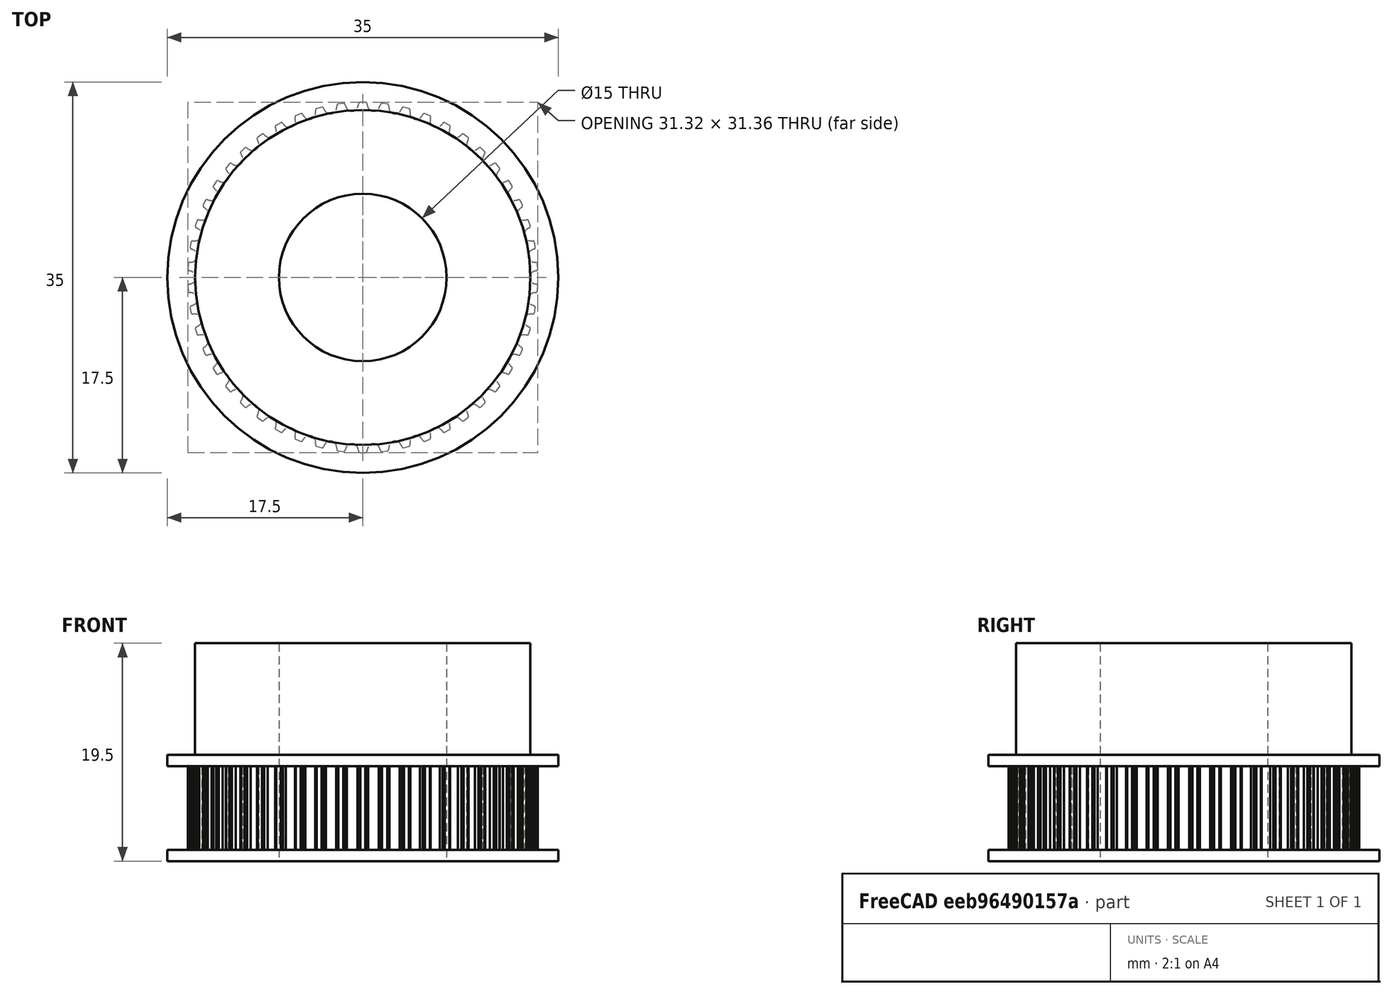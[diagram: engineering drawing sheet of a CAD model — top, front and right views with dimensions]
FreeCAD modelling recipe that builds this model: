
FCSTD DOCUMENT  (FreeCAD 1.0R39319 (Git))
Label: GT2_50
License: All rights reserved
LicenseURL: https://en.wikipedia.org/wiki/All_rights_reserved
objects: Sketcher::SketchObject×4, PartDesign::Pad×4, PartDesign::Body×1
note: 21 computed .brp shape members not serialized (recipe doc carries the construction recipe); baked Part::Feature solids carry a one-line shape summary decoded from their .brp

FEATURE [Sketcher::SketchObject] SketchGear
  ArcFitTolerance = 1e-06
  FullyConstrained = false
  MakeInternals = false
  MapMode = 5
  Placement = pos=(0,0,1) rot=(0,0,1;0rad)
  sketch-geometry (301):
    g0: ArcOfCircle CenterX=15.5115 CenterY=-0.75 CenterZ=0 NormalX=0 NormalY=0 NormalZ=1 AngleXU=1.11e-14 Radius=0.15 StartAngle=0 EndAngle=1.5708
    g1: ArcOfCircle CenterX=15.8575 CenterY=0.82798 CenterZ=0 NormalX=0 NormalY=0 NormalZ=-1 AngleXU=-1.3331 Radius=1.46929 StartAngle=0 EndAngle=0.255762
    g2: ArcOfCircle CenterX=15.4709 CenterY=0 CenterZ=0 NormalX=0 NormalY=0 NormalZ=-1 AngleXU=-0.984764 Radius=0.559359 StartAngle=0 EndAngle=1.96953
    g3: ArcOfCircle CenterX=15.8575 CenterY=-0.82798 CenterZ=0 NormalX=0 NormalY=0 NormalZ=-1 AngleXU=1.07734 Radius=1.46929 StartAngle=0 EndAngle=0.255762
    g4: ArcOfCircle CenterX=15.5115 CenterY=0.75 CenterZ=0 NormalX=0 NormalY=0 NormalZ=1 AngleXU=-1.5708 Radius=0.15 StartAngle=0 EndAngle=1.5708
    g5: LineSegment StartX=15.6615 StartY=0.75 StartZ=0 EndX=15.632 EndY=1.21882 EndZ=0
    g6: ArcOfCircle CenterX=15.4832 CenterY=1.20002 CenterZ=0 NormalX=0 NormalY=0 NormalZ=1 AngleXU=0.125664 Radius=0.15 StartAngle=0 EndAngle=1.5708
    g7: ArcOfCircle CenterX=15.6286 CenterY=2.80892 CenterZ=0 NormalX=0 NormalY=0 NormalZ=-1 AngleXU=-1.45876 Radius=1.46929 StartAngle=0 EndAngle=0.255762
    g8: ArcOfCircle CenterX=15.3489 CenterY=1.93901 CenterZ=0 NormalX=0 NormalY=0 NormalZ=-1 AngleXU=-1.11043 Radius=0.559359 StartAngle=0 EndAngle=1.96953
    g9: ArcOfCircle CenterX=15.8362 CenterY=1.16602 CenterZ=0 NormalX=0 NormalY=0 NormalZ=-1 AngleXU=0.951674 Radius=1.46929 StartAngle=0 EndAngle=0.255762
    g10: ArcOfCircle CenterX=15.2952 CenterY=2.68819 CenterZ=0 NormalX=0 NormalY=0 NormalZ=1 AngleXU=-1.44513 Radius=0.15 StartAngle=0 EndAngle=1.5708
    g11: LineSegment StartX=15.444 StartY=2.70699 StartZ=0 EndX=15.356 EndY=3.16842 EndZ=0
    g12: ArcOfCircle CenterX=15.2107 CenterY=3.13111 CenterZ=0 NormalX=0 NormalY=0 NormalZ=1 AngleXU=0.251327 Radius=0.15 StartAngle=0 EndAngle=1.5708
    g13: ArcOfCircle CenterX=15.1534 CenterY=4.74556 CenterZ=0 NormalX=0 NormalY=0 NormalZ=-1 AngleXU=-1.58443 Radius=1.46929 StartAngle=0 EndAngle=0.255762
    g14: ArcOfCircle CenterX=14.9848 CenterY=3.84744 CenterZ=0 NormalX=0 NormalY=0 NormalZ=-1 AngleXU=-1.23609 Radius=0.559359 StartAngle=0 EndAngle=1.96953
    g15: ArcOfCircle CenterX=15.5652 CenterY=3.14162 CenterZ=0 NormalX=0 NormalY=0 NormalZ=-1 AngleXU=0.82601 Radius=1.46929 StartAngle=0 EndAngle=0.255762
    g16: ArcOfCircle CenterX=14.8377 CenterY=4.58399 CenterZ=0 NormalX=0 NormalY=0 NormalZ=1 AngleXU=-1.31947 Radius=0.15 StartAngle=0 EndAngle=1.5708
    g17: LineSegment StartX=14.9829 StartY=4.62129 StartZ=0 EndX=14.8378 EndY=5.06805 EndZ=0
    g18: ArcOfCircle CenterX=14.6983 CenterY=5.01283 CenterZ=0 NormalX=0 NormalY=0 NormalZ=1 AngleXU=0.376991 Radius=0.15 StartAngle=0 EndAngle=1.5708
    g19: ArcOfCircle CenterX=14.4391 CenterY=6.60736 CenterZ=0 NormalX=0 NormalY=0 NormalZ=-1 AngleXU=-1.71009 Radius=1.46929 StartAngle=0 EndAngle=0.255762
    g20: ArcOfCircle CenterX=14.3844 CenterY=5.6952 CenterZ=0 NormalX=0 NormalY=0 NormalZ=-1 AngleXU=-1.36175 Radius=0.559359 StartAngle=0 EndAngle=1.96953
    g21: ArcOfCircle CenterX=15.0487 CenterY=5.06768 CenterZ=0 NormalX=0 NormalY=0 NormalZ=-1 AngleXU=0.700346 Radius=1.46929 StartAngle=0 EndAngle=0.255762
    g22: ArcOfCircle CenterX=14.1461 CenterY=6.40749 CenterZ=0 NormalX=0 NormalY=0 NormalZ=1 AngleXU=-1.19381 Radius=0.15 StartAngle=0 EndAngle=1.5708
    g23: LineSegment StartX=14.2856 StartY=6.46271 StartZ=0 EndX=14.0856 EndY=6.88775 EndZ=0
    g24: ArcOfCircle CenterX=13.9541 CenterY=6.81549 CenterZ=0 NormalX=0 NormalY=0 NormalZ=1 AngleXU=0.502655 Radius=0.15 StartAngle=0 EndAngle=1.5708
    g25: ArcOfCircle CenterX=13.4971 CenterY=8.36496 CenterZ=0 NormalX=0 NormalY=0 NormalZ=-1 AngleXU=-1.83575 Radius=1.46929 StartAngle=0 EndAngle=0.255762
    g26: ArcOfCircle CenterX=13.5572 CenterY=7.45314 CenterZ=0 NormalX=0 NormalY=0 NormalZ=-1 AngleXU=-1.48742 Radius=0.559359 StartAngle=0 EndAngle=1.96953
    g27: ArcOfCircle CenterX=14.2949 CenterY=6.91383 CenterZ=0 NormalX=0 NormalY=0 NormalZ=-1 AngleXU=0.574683 Radius=1.46929 StartAngle=0 EndAngle=0.255762
    g28: ArcOfCircle CenterX=13.2315 CenterY=8.12995 CenterZ=0 NormalX=0 NormalY=0 NormalZ=1 AngleXU=-1.06814 Radius=0.15 StartAngle=0 EndAngle=1.5708
    g29: LineSegment StartX=13.363 StartY=8.20221 StartZ=0 EndX=13.1113 EndY=8.59883 EndZ=0
    g30: ArcOfCircle CenterX=12.9899 CenterY=8.51066 CenterZ=0 NormalX=0 NormalY=0 NormalZ=1 AngleXU=0.628319 Radius=0.15 StartAngle=0 EndAngle=1.5708
    g31: ArcOfCircle CenterX=12.3423 CenterY=9.99063 CenterZ=0 NormalX=0 NormalY=0 NormalZ=-1 AngleXU=-1.96142 Radius=1.46929 StartAngle=0 EndAngle=0.255762
    g32: ArcOfCircle CenterX=12.5162 CenterY=9.09354 CenterZ=0 NormalX=0 NormalY=0 NormalZ=-1 AngleXU=-1.61308 Radius=0.559359 StartAngle=0 EndAngle=1.96953
    g33: ArcOfCircle CenterX=13.3156 CenterY=8.65093 CenterZ=0 NormalX=0 NormalY=0 NormalZ=-1 AngleXU=0.449019 Radius=1.46929 StartAngle=0 EndAngle=0.255762
    g34: ArcOfCircle CenterX=12.1082 CenterY=9.72419 CenterZ=0 NormalX=0 NormalY=0 NormalZ=1 AngleXU=-0.942478 Radius=0.15 StartAngle=0 EndAngle=1.5708
    g35: LineSegment StartX=12.2296 StartY=9.81236 StartZ=0 EndX=11.9301 EndY=10.1743 EndZ=0
    g36: ArcOfCircle CenterX=11.8208 CenterY=10.0716 CenterZ=0 NormalX=0 NormalY=0 NormalZ=1 AngleXU=0.753982 Radius=0.15 StartAngle=0 EndAngle=1.5708
    g37: ArcOfCircle CenterX=10.9928 CenterY=11.4588 CenterZ=0 NormalX=0 NormalY=0 NormalZ=-1 AngleXU=-2.08708 Radius=1.46929 StartAngle=0 EndAngle=0.255762
    g38: ArcOfCircle CenterX=11.2778 CenterY=10.5905 CenterZ=0 NormalX=0 NormalY=0 NormalZ=-1 AngleXU=-1.73875 Radius=0.559359 StartAngle=0 EndAngle=1.96953
    g39: ArcOfCircle CenterX=12.1264 CenterY=10.2516 CenterZ=0 NormalX=0 NormalY=0 NormalZ=-1 AngleXU=0.323355 Radius=1.46929 StartAngle=0 EndAngle=0.255762
    g40: ArcOfCircle CenterX=10.794 CenterY=11.1651 CenterZ=0 NormalX=0 NormalY=0 NormalZ=1 AngleXU=-0.816814 Radius=0.15 StartAngle=0 EndAngle=1.5708
    g41: LineSegment StartX=10.9033 StartY=11.2678 StartZ=0 EndX=10.5609 EndY=11.5893 EndZ=0
    g42: ArcOfCircle CenterX=10.4653 CenterY=11.4737 CenterZ=0 NormalX=0 NormalY=0 NormalZ=1 AngleXU=0.879646 Radius=0.15 StartAngle=0 EndAngle=1.5708
    g43: ArcOfCircle CenterX=9.46996 CenterY=12.7462 CenterZ=0 NormalX=0 NormalY=0 NormalZ=-1 AngleXU=-2.21275 Radius=1.46929 StartAngle=0 EndAngle=0.255762
    g44: ArcOfCircle CenterX=9.86149 CenterY=11.9205 CenterZ=0 NormalX=0 NormalY=0 NormalZ=-1 AngleXU=-1.86441 Radius=0.559359 StartAngle=0 EndAngle=1.96953
    g45: ArcOfCircle CenterX=10.7459 CenterY=11.6906 CenterZ=0 NormalX=0 NormalY=0 NormalZ=-1 AngleXU=0.197692 Radius=1.46929 StartAngle=0 EndAngle=0.255762
    g46: ArcOfCircle CenterX=9.30951 CenterY=12.4299 CenterZ=0 NormalX=0 NormalY=0 NormalZ=1 AngleXU=-0.69115 Radius=0.15 StartAngle=0 EndAngle=1.5708
    g47: LineSegment StartX=9.40513 StartY=12.5455 StartZ=0 EndX=9.02509 EndY=12.8216 EndZ=0
    g48: ArcOfCircle CenterX=8.94472 CenterY=12.6949 CenterZ=0 NormalX=0 NormalY=0 NormalZ=1 AngleXU=1.00531 Radius=0.15 StartAngle=0 EndAngle=1.5708
    g49: ArcOfCircle CenterX=7.79777 CenterY=13.8326 CenterZ=0 NormalX=0 NormalY=0 NormalZ=-1 AngleXU=-2.33841 Radius=1.46929 StartAngle=0 EndAngle=0.255762
    g50: ArcOfCircle CenterX=8.2897 CenterY=13.0625 CenterZ=0 NormalX=0 NormalY=0 NormalZ=-1 AngleXU=-1.99007 Radius=0.559359 StartAngle=0 EndAngle=1.96953
    g51: ArcOfCircle CenterX=9.19594 CenterY=12.9452 CenterZ=0 NormalX=0 NormalY=0 NormalZ=-1 AngleXU=0.0720278 Radius=1.46929 StartAngle=0 EndAngle=0.255762
    g52: ArcOfCircle CenterX=7.67823 CenterY=13.4987 CenterZ=0 NormalX=0 NormalY=0 NormalZ=1 AngleXU=-0.565487 Radius=0.15 StartAngle=0 EndAngle=1.5708
    g53: LineSegment StartX=7.7586 StartY=13.6253 StartZ=0 EndX=7.34696 EndY=13.8516 EndZ=0
    g54: ArcOfCircle CenterX=7.28309 CenterY=13.7159 CenterZ=0 NormalX=0 NormalY=0 NormalZ=1 AngleXU=1.13097 Radius=0.15 StartAngle=0 EndAngle=1.5708
    g55: ArcOfCircle CenterX=6.0026 CenterY=14.7008 CenterZ=0 NormalX=0 NormalY=0 NormalZ=-1 AngleXU=-2.46407 Radius=1.46929 StartAngle=0 EndAngle=0.255762
    g56: ArcOfCircle CenterX=6.58717 CenterY=13.9984 CenterZ=0 NormalX=0 NormalY=0 NormalZ=-1 AngleXU=-2.11574 Radius=0.559359 StartAngle=0 EndAngle=1.96953
    g57: ArcOfCircle CenterX=7.50096 CenterY=13.9957 CenterZ=0 NormalX=0 NormalY=0 NormalZ=-1 AngleXU=-0.0536359 Radius=1.46929 StartAngle=0 EndAngle=0.255762
    g58: ArcOfCircle CenterX=5.92585 CenterY=14.3546 CenterZ=0 NormalX=0 NormalY=0 NormalZ=1 AngleXU=-0.439823 Radius=0.15 StartAngle=0 EndAngle=1.5708
    g59: LineSegment StartX=5.98972 StartY=14.4903 StartZ=0 EndX=5.55296 EndY=14.6632 EndZ=0
    g60: ArcOfCircle CenterX=5.50661 CenterY=14.5205 CenterZ=0 NormalX=0 NormalY=0 NormalZ=1 AngleXU=1.25664 Radius=0.15 StartAngle=0 EndAngle=1.5708
    g61: ArcOfCircle CenterX=4.11277 CenterY=15.3372 CenterZ=0 NormalX=0 NormalY=0 NormalZ=-1 AngleXU=-2.58974 Radius=1.46929 StartAngle=0 EndAngle=0.255762
    g62: ArcOfCircle CenterX=4.78076 CenterY=14.7137 CenterZ=0 NormalX=0 NormalY=0 NormalZ=-1 AngleXU=-2.2414 Radius=0.559359 StartAngle=0 EndAngle=1.96953
    g63: ArcOfCircle CenterX=5.68768 CenterY=14.8255 CenterZ=0 NormalX=0 NormalY=0 NormalZ=-1 AngleXU=-0.1793 Radius=1.46929 StartAngle=0 EndAngle=0.255762
    g64: ArcOfCircle CenterX=4.08002 CenterY=14.9841 CenterZ=0 NormalX=0 NormalY=0 NormalZ=1 AngleXU=-0.314159 Radius=0.15 StartAngle=0 EndAngle=1.5708
    g65: LineSegment StartX=4.12638 StartY=15.1267 StartZ=0 EndX=3.67139 EndY=15.2436 EndZ=0
    g66: ArcOfCircle CenterX=3.64328 CenterY=15.0962 CenterZ=0 NormalX=0 NormalY=0 NormalZ=1 AngleXU=1.3823 Radius=0.15 StartAngle=0 EndAngle=1.5708
    g67: ArcOfCircle CenterX=2.15808 CenterY=15.7317 CenterZ=0 NormalX=0 NormalY=0 NormalZ=-1 AngleXU=-2.7154 Radius=1.46929 StartAngle=0 EndAngle=0.255762
    g68: ArcOfCircle CenterX=2.89895 CenterY=15.1968 CenterZ=0 NormalX=0 NormalY=0 NormalZ=-1 AngleXU=-2.36706 Radius=0.559359 StartAngle=0 EndAngle=1.96953
    g69: ArcOfCircle CenterX=3.78471 CenterY=15.4214 CenterZ=0 NormalX=0 NormalY=0 NormalZ=-1 AngleXU=-0.304963 Radius=1.46929 StartAngle=0 EndAngle=0.255762
    g70: ArcOfCircle CenterX=2.16985 CenterY=15.3773 CenterZ=0 NormalX=0 NormalY=0 NormalZ=1 AngleXU=-0.188496 Radius=0.15 StartAngle=0 EndAngle=1.5708
    g71: LineSegment StartX=2.19796 StartY=15.5246 StartZ=0 EndX=1.73191 EndY=15.5835 EndZ=0
    g72: ArcOfCircle CenterX=1.72249 CenterY=15.4338 CenterZ=0 NormalX=0 NormalY=0 NormalZ=1 AngleXU=1.50796 Radius=0.15 StartAngle=0 EndAngle=1.5708
    g73: ArcOfCircle CenterX=0.169352 CenterY=15.8782 CenterZ=0 NormalX=0 NormalY=0 NormalZ=-1 AngleXU=-2.84106 Radius=1.46929 StartAngle=0 EndAngle=0.255762
    g74: ArcOfCircle CenterX=0.971423 CenterY=15.4403 CenterZ=0 NormalX=0 NormalY=0 NormalZ=-1 AngleXU=-2.49273 Radius=0.559359 StartAngle=0 EndAngle=1.96953
    g75: ArcOfCircle CenterX=1.82204 CenterY=15.7742 CenterZ=0 NormalX=0 NormalY=0 NormalZ=-1 AngleXU=-0.430627 Radius=1.46929 StartAngle=0 EndAngle=0.255762
    g76: ArcOfCircle CenterX=0.225455 CenterY=15.528 CenterZ=0 NormalX=0 NormalY=0 NormalZ=1 AngleXU=-0.0628319 Radius=0.15 StartAngle=0 EndAngle=1.5708
    g77: LineSegment StartX=0.234873 StartY=15.6777 StartZ=0 EndX=-0.234873 EndY=15.6777 EndZ=0
    g78: ArcOfCircle CenterX=-0.225455 CenterY=15.528 CenterZ=0 NormalX=0 NormalY=0 NormalZ=1 AngleXU=1.63363 Radius=0.15 StartAngle=0 EndAngle=1.5708
    g79: ArcOfCircle CenterX=-1.82204 CenterY=15.7742 CenterZ=0 NormalX=0 NormalY=0 NormalZ=-1 AngleXU=-2.96673 Radius=1.46929 StartAngle=0 EndAngle=0.255762
    g80: ArcOfCircle CenterX=-0.971423 CenterY=15.4403 CenterZ=0 NormalX=0 NormalY=0 NormalZ=-1 AngleXU=-2.61839 Radius=0.559359 StartAngle=0 EndAngle=1.96953
    g81: ArcOfCircle CenterX=-0.169352 CenterY=15.8782 CenterZ=0 NormalX=0 NormalY=0 NormalZ=-1 AngleXU=-0.556291 Radius=1.46929 StartAngle=0 EndAngle=0.255762
    g82: ArcOfCircle CenterX=-1.72249 CenterY=15.4338 CenterZ=0 NormalX=0 NormalY=0 NormalZ=1 AngleXU=0.0628319 Radius=0.15 StartAngle=0 EndAngle=1.5708
    g83: LineSegment StartX=-1.73191 StartY=15.5835 StartZ=0 EndX=-2.19796 EndY=15.5246 EndZ=0
    g84: ArcOfCircle CenterX=-2.16985 CenterY=15.3773 CenterZ=0 NormalX=0 NormalY=0 NormalZ=1 AngleXU=1.75929 Radius=0.15 StartAngle=0 EndAngle=1.5708
    g85: ArcOfCircle CenterX=-3.78471 CenterY=15.4214 CenterZ=0 NormalX=0 NormalY=0 NormalZ=-1 AngleXU=-3.09239 Radius=1.46929 StartAngle=0 EndAngle=0.255762
    g86: ArcOfCircle CenterX=-2.89895 CenterY=15.1968 CenterZ=0 NormalX=0 NormalY=0 NormalZ=-1 AngleXU=-2.74406 Radius=0.559359 StartAngle=0 EndAngle=1.96953
    g87: ArcOfCircle CenterX=-2.15808 CenterY=15.7317 CenterZ=0 NormalX=0 NormalY=0 NormalZ=-1 AngleXU=-0.681954 Radius=1.46929 StartAngle=0 EndAngle=0.255762
    g88: ArcOfCircle CenterX=-3.64328 CenterY=15.0962 CenterZ=0 NormalX=0 NormalY=0 NormalZ=1 AngleXU=0.188496 Radius=0.15 StartAngle=0 EndAngle=1.5708
    g89: LineSegment StartX=-3.67139 StartY=15.2436 StartZ=0 EndX=-4.12638 EndY=15.1267 EndZ=0
    g90: ArcOfCircle CenterX=-4.08002 CenterY=14.9841 CenterZ=0 NormalX=0 NormalY=0 NormalZ=1 AngleXU=1.88496 Radius=0.15 StartAngle=0 EndAngle=1.5708
    g91: ArcOfCircle CenterX=-5.68768 CenterY=14.8255 CenterZ=0 NormalX=0 NormalY=0 NormalZ=-1 AngleXU=3.06513 Radius=1.46929 StartAngle=0 EndAngle=0.255762
    g92: ArcOfCircle CenterX=-4.78076 CenterY=14.7137 CenterZ=0 NormalX=0 NormalY=0 NormalZ=-1 AngleXU=-2.86972 Radius=0.559359 StartAngle=0 EndAngle=1.96953
    g93: ArcOfCircle CenterX=-4.11277 CenterY=15.3372 CenterZ=0 NormalX=0 NormalY=0 NormalZ=-1 AngleXU=-0.807618 Radius=1.46929 StartAngle=0 EndAngle=0.255762
    g94: ArcOfCircle CenterX=-5.50661 CenterY=14.5205 CenterZ=0 NormalX=0 NormalY=0 NormalZ=1 AngleXU=0.314159 Radius=0.15 StartAngle=0 EndAngle=1.5708
    g95: LineSegment StartX=-5.55296 StartY=14.6632 StartZ=0 EndX=-5.98972 EndY=14.4903 EndZ=0
    g96: ArcOfCircle CenterX=-5.92585 CenterY=14.3546 CenterZ=0 NormalX=0 NormalY=0 NormalZ=1 AngleXU=2.01062 Radius=0.15 StartAngle=0 EndAngle=1.5708
    g97: ArcOfCircle CenterX=-7.50096 CenterY=13.9957 CenterZ=0 NormalX=0 NormalY=0 NormalZ=-1 AngleXU=2.93947 Radius=1.46929 StartAngle=0 EndAngle=0.255762
    g98: ArcOfCircle CenterX=-6.58717 CenterY=13.9984 CenterZ=0 NormalX=0 NormalY=0 NormalZ=-1 AngleXU=-2.99538 Radius=0.559359 StartAngle=0 EndAngle=1.96953
    g99: ArcOfCircle CenterX=-6.0026 CenterY=14.7008 CenterZ=0 NormalX=0 NormalY=0 NormalZ=-1 AngleXU=-0.933282 Radius=1.46929 StartAngle=0 EndAngle=0.255762
    g100: ArcOfCircle CenterX=-7.28309 CenterY=13.7159 CenterZ=0 NormalX=0 NormalY=0 NormalZ=1 AngleXU=0.439823 Radius=0.15 StartAngle=0 EndAngle=1.5708
    g101: LineSegment StartX=-7.34696 StartY=13.8516 StartZ=0 EndX=-7.7586 EndY=13.6253 EndZ=0
    g102: ArcOfCircle CenterX=-7.67823 CenterY=13.4987 CenterZ=0 NormalX=0 NormalY=0 NormalZ=1 AngleXU=2.13628 Radius=0.15 StartAngle=0 EndAngle=1.5708
    g103: ArcOfCircle CenterX=-9.19594 CenterY=12.9452 CenterZ=0 NormalX=0 NormalY=0 NormalZ=-1 AngleXU=2.8138 Radius=1.46929 StartAngle=0 EndAngle=0.255762
    g104: ArcOfCircle CenterX=-8.2897 CenterY=13.0625 CenterZ=0 NormalX=0 NormalY=0 NormalZ=-1 AngleXU=-3.12105 Radius=0.559359 StartAngle=0 EndAngle=1.96953
    g105: ArcOfCircle CenterX=-7.79777 CenterY=13.8326 CenterZ=0 NormalX=0 NormalY=0 NormalZ=-1 AngleXU=-1.05895 Radius=1.46929 StartAngle=0 EndAngle=0.255762
    g106: ArcOfCircle CenterX=-8.94472 CenterY=12.6949 CenterZ=0 NormalX=0 NormalY=0 NormalZ=1 AngleXU=0.565487 Radius=0.15 StartAngle=0 EndAngle=1.5708
    g107: LineSegment StartX=-9.02509 StartY=12.8216 StartZ=0 EndX=-9.40513 EndY=12.5455 EndZ=0
    g108: ArcOfCircle CenterX=-9.30951 CenterY=12.4299 CenterZ=0 NormalX=0 NormalY=0 NormalZ=1 AngleXU=2.26195 Radius=0.15 StartAngle=0 EndAngle=1.5708
    g109: ArcOfCircle CenterX=-10.7459 CenterY=11.6906 CenterZ=0 NormalX=0 NormalY=0 NormalZ=-1 AngleXU=2.68814 Radius=1.46929 StartAngle=0 EndAngle=0.255762
    g110: ArcOfCircle CenterX=-9.86149 CenterY=11.9205 CenterZ=0 NormalX=0 NormalY=0 NormalZ=-1 AngleXU=3.03648 Radius=0.559359 StartAngle=0 EndAngle=1.96953
    g111: ArcOfCircle CenterX=-9.46996 CenterY=12.7462 CenterZ=0 NormalX=0 NormalY=0 NormalZ=-1 AngleXU=-1.18461 Radius=1.46929 StartAngle=0 EndAngle=0.255762
    g112: ArcOfCircle CenterX=-10.4653 CenterY=11.4737 CenterZ=0 NormalX=0 NormalY=0 NormalZ=1 AngleXU=0.69115 Radius=0.15 StartAngle=0 EndAngle=1.5708
    g113: LineSegment StartX=-10.5609 StartY=11.5893 StartZ=0 EndX=-10.9033 EndY=11.2678 EndZ=0
    g114: ArcOfCircle CenterX=-10.794 CenterY=11.1651 CenterZ=0 NormalX=0 NormalY=0 NormalZ=1 AngleXU=2.38761 Radius=0.15 StartAngle=0 EndAngle=1.5708
    g115: ArcOfCircle CenterX=-12.1264 CenterY=10.2516 CenterZ=0 NormalX=0 NormalY=0 NormalZ=-1 AngleXU=2.56248 Radius=1.46929 StartAngle=0 EndAngle=0.255762
    g116: ArcOfCircle CenterX=-11.2778 CenterY=10.5905 CenterZ=0 NormalX=0 NormalY=0 NormalZ=-1 AngleXU=2.91081 Radius=0.559359 StartAngle=0 EndAngle=1.96953
    g117: ArcOfCircle CenterX=-10.9928 CenterY=11.4588 CenterZ=0 NormalX=0 NormalY=0 NormalZ=-1 AngleXU=-1.31027 Radius=1.46929 StartAngle=0 EndAngle=0.255762
    g118: ArcOfCircle CenterX=-11.8208 CenterY=10.0716 CenterZ=0 NormalX=0 NormalY=0 NormalZ=1 AngleXU=0.816814 Radius=0.15 StartAngle=0 EndAngle=1.5708
    g119: LineSegment StartX=-11.9301 StartY=10.1743 StartZ=0 EndX=-12.2296 EndY=9.81236 EndZ=0
    g120: ArcOfCircle CenterX=-12.1082 CenterY=9.72419 CenterZ=0 NormalX=0 NormalY=0 NormalZ=1 AngleXU=2.51327 Radius=0.15 StartAngle=0 EndAngle=1.5708
    g121: ArcOfCircle CenterX=-13.3156 CenterY=8.65093 CenterZ=0 NormalX=0 NormalY=0 NormalZ=-1 AngleXU=2.43681 Radius=1.46929 StartAngle=0 EndAngle=0.255762
    g122: ArcOfCircle CenterX=-12.5162 CenterY=9.09354 CenterZ=0 NormalX=0 NormalY=0 NormalZ=-1 AngleXU=2.78515 Radius=0.559359 StartAngle=0 EndAngle=1.96953
    g123: ArcOfCircle CenterX=-12.3423 CenterY=9.99063 CenterZ=0 NormalX=0 NormalY=0 NormalZ=-1 AngleXU=-1.43594 Radius=1.46929 StartAngle=0 EndAngle=0.255762
    g124: ArcOfCircle CenterX=-12.9899 CenterY=8.51066 CenterZ=0 NormalX=0 NormalY=0 NormalZ=1 AngleXU=0.942478 Radius=0.15 StartAngle=0 EndAngle=1.5708
    g125: LineSegment StartX=-13.1113 StartY=8.59883 StartZ=0 EndX=-13.363 EndY=8.20221 EndZ=0
    g126: ArcOfCircle CenterX=-13.2315 CenterY=8.12995 CenterZ=0 NormalX=0 NormalY=0 NormalZ=1 AngleXU=2.63894 Radius=0.15 StartAngle=0 EndAngle=1.5708
    g127: ArcOfCircle CenterX=-14.2949 CenterY=6.91383 CenterZ=0 NormalX=0 NormalY=0 NormalZ=-1 AngleXU=2.31115 Radius=1.46929 StartAngle=0 EndAngle=0.255762
    g128: ArcOfCircle CenterX=-13.5572 CenterY=7.45314 CenterZ=0 NormalX=0 NormalY=0 NormalZ=-1 AngleXU=2.65948 Radius=0.559359 StartAngle=0 EndAngle=1.96953
    g129: ArcOfCircle CenterX=-13.4971 CenterY=8.36496 CenterZ=0 NormalX=0 NormalY=0 NormalZ=-1 AngleXU=-1.5616 Radius=1.46929 StartAngle=0 EndAngle=0.255762
    g130: ArcOfCircle CenterX=-13.9541 CenterY=6.81549 CenterZ=0 NormalX=0 NormalY=0 NormalZ=1 AngleXU=1.06814 Radius=0.15 StartAngle=0 EndAngle=1.5708
    g131: LineSegment StartX=-14.0856 StartY=6.88775 StartZ=0 EndX=-14.2856 EndY=6.46271 EndZ=0
    g132: ArcOfCircle CenterX=-14.1461 CenterY=6.40749 CenterZ=0 NormalX=0 NormalY=0 NormalZ=1 AngleXU=2.7646 Radius=0.15 StartAngle=0 EndAngle=1.5708
    g133: ArcOfCircle CenterX=-15.0487 CenterY=5.06768 CenterZ=0 NormalX=0 NormalY=0 NormalZ=-1 AngleXU=2.18548 Radius=1.46929 StartAngle=0 EndAngle=0.255762
    g134: ArcOfCircle CenterX=-14.3844 CenterY=5.6952 CenterZ=0 NormalX=0 NormalY=0 NormalZ=-1 AngleXU=2.53382 Radius=0.559359 StartAngle=0 EndAngle=1.96953
    g135: ArcOfCircle CenterX=-14.4391 CenterY=6.60736 CenterZ=0 NormalX=0 NormalY=0 NormalZ=-1 AngleXU=-1.68726 Radius=1.46929 StartAngle=0 EndAngle=0.255762
    g136: ArcOfCircle CenterX=-14.6983 CenterY=5.01283 CenterZ=0 NormalX=0 NormalY=0 NormalZ=1 AngleXU=1.19381 Radius=0.15 StartAngle=0 EndAngle=1.5708
    g137: LineSegment StartX=-14.8378 StartY=5.06805 StartZ=0 EndX=-14.9829 EndY=4.62129 EndZ=0
    g138: ArcOfCircle CenterX=-14.8377 CenterY=4.58399 CenterZ=0 NormalX=0 NormalY=0 NormalZ=1 AngleXU=2.89027 Radius=0.15 StartAngle=0 EndAngle=1.5708
    g139: ArcOfCircle CenterX=-15.5652 CenterY=3.14162 CenterZ=0 NormalX=0 NormalY=0 NormalZ=-1 AngleXU=2.05982 Radius=1.46929 StartAngle=0 EndAngle=0.255762
    g140: ArcOfCircle CenterX=-14.9848 CenterY=3.84744 CenterZ=0 NormalX=0 NormalY=0 NormalZ=-1 AngleXU=2.40816 Radius=0.559359 StartAngle=0 EndAngle=1.96953
    g141: ArcOfCircle CenterX=-15.1534 CenterY=4.74556 CenterZ=0 NormalX=0 NormalY=0 NormalZ=-1 AngleXU=-1.81293 Radius=1.46929 StartAngle=0 EndAngle=0.255762
    g142: ArcOfCircle CenterX=-15.2107 CenterY=3.13111 CenterZ=0 NormalX=0 NormalY=0 NormalZ=1 AngleXU=1.31947 Radius=0.15 StartAngle=0 EndAngle=1.5708
    g143: LineSegment StartX=-15.356 StartY=3.16842 StartZ=0 EndX=-15.444 EndY=2.70699 EndZ=0
    g144: ArcOfCircle CenterX=-15.2952 CenterY=2.68819 CenterZ=0 NormalX=0 NormalY=0 NormalZ=1 AngleXU=3.01593 Radius=0.15 StartAngle=0 EndAngle=1.5708
    g145: ArcOfCircle CenterX=-15.8362 CenterY=1.16602 CenterZ=0 NormalX=0 NormalY=0 NormalZ=-1 AngleXU=1.93416 Radius=1.46929 StartAngle=0 EndAngle=0.255762
    g146: ArcOfCircle CenterX=-15.3489 CenterY=1.93901 CenterZ=0 NormalX=0 NormalY=0 NormalZ=-1 AngleXU=2.28249 Radius=0.559359 StartAngle=0 EndAngle=1.96953
    g147: ArcOfCircle CenterX=-15.6286 CenterY=2.80892 CenterZ=0 NormalX=0 NormalY=0 NormalZ=-1 AngleXU=-1.93859 Radius=1.46929 StartAngle=0 EndAngle=0.255762
    g148: ArcOfCircle CenterX=-15.4832 CenterY=1.20002 CenterZ=0 NormalX=0 NormalY=0 NormalZ=1 AngleXU=1.44513 Radius=0.15 StartAngle=0 EndAngle=1.5708
    g149: LineSegment StartX=-15.632 StartY=1.21882 StartZ=0 EndX=-15.6615 EndY=0.75 EndZ=0
    g150: ArcOfCircle CenterX=-15.5115 CenterY=0.75 CenterZ=0 NormalX=0 NormalY=0 NormalZ=1 AngleXU=-3.14159 Radius=0.15 StartAngle=0 EndAngle=1.5708
    g151: ArcOfCircle CenterX=-15.8575 CenterY=-0.82798 CenterZ=0 NormalX=0 NormalY=0 NormalZ=-1 AngleXU=1.80849 Radius=1.46929 StartAngle=0 EndAngle=0.255762
    g152: ArcOfCircle CenterX=-15.4709 CenterY=1.8e-15 CenterZ=0 NormalX=0 NormalY=0 NormalZ=-1 AngleXU=2.15683 Radius=0.559359 StartAngle=0 EndAngle=1.96953
    g153: ArcOfCircle CenterX=-15.8575 CenterY=0.82798 CenterZ=0 NormalX=0 NormalY=0 NormalZ=-1 AngleXU=-2.06426 Radius=1.46929 StartAngle=0 EndAngle=0.255762
    g154: ArcOfCircle CenterX=-15.5115 CenterY=-0.75 CenterZ=0 NormalX=0 NormalY=0 NormalZ=1 AngleXU=1.5708 Radius=0.15 StartAngle=0 EndAngle=1.5708
    g155: LineSegment StartX=-15.6615 StartY=-0.75 StartZ=0 EndX=-15.632 EndY=-1.21882 EndZ=0
    g156: ArcOfCircle CenterX=-15.4832 CenterY=-1.20002 CenterZ=0 NormalX=0 NormalY=0 NormalZ=1 AngleXU=-3.01593 Radius=0.15 StartAngle=0 EndAngle=1.5708
    g157: ArcOfCircle CenterX=-15.6286 CenterY=-2.80892 CenterZ=0 NormalX=0 NormalY=0 NormalZ=-1 AngleXU=1.68283 Radius=1.46929 StartAngle=0 EndAngle=0.255762
    g158: ArcOfCircle CenterX=-15.3489 CenterY=-1.93901 CenterZ=0 NormalX=0 NormalY=0 NormalZ=-1 AngleXU=2.03117 Radius=0.559359 StartAngle=0 EndAngle=1.96953
    g159: ArcOfCircle CenterX=-15.8362 CenterY=-1.16602 CenterZ=0 NormalX=0 NormalY=0 NormalZ=-1 AngleXU=-2.18992 Radius=1.46929 StartAngle=0 EndAngle=0.255762
    g160: ArcOfCircle CenterX=-15.2952 CenterY=-2.68819 CenterZ=0 NormalX=0 NormalY=0 NormalZ=1 AngleXU=1.69646 Radius=0.15 StartAngle=0 EndAngle=1.5708
    g161: LineSegment StartX=-15.444 StartY=-2.70699 StartZ=0 EndX=-15.356 EndY=-3.16842 EndZ=0
    g162: ArcOfCircle CenterX=-15.2107 CenterY=-3.13111 CenterZ=0 NormalX=0 NormalY=0 NormalZ=1 AngleXU=-2.89027 Radius=0.15 StartAngle=0 EndAngle=1.5708
    g163: ArcOfCircle CenterX=-15.1534 CenterY=-4.74556 CenterZ=0 NormalX=0 NormalY=0 NormalZ=-1 AngleXU=1.55717 Radius=1.46929 StartAngle=0 EndAngle=0.255762
    g164: ArcOfCircle CenterX=-14.9848 CenterY=-3.84744 CenterZ=0 NormalX=0 NormalY=0 NormalZ=-1 AngleXU=1.9055 Radius=0.559359 StartAngle=0 EndAngle=1.96953
    g165: ArcOfCircle CenterX=-15.5652 CenterY=-3.14162 CenterZ=0 NormalX=0 NormalY=0 NormalZ=-1 AngleXU=-2.31558 Radius=1.46929 StartAngle=0 EndAngle=0.255762
    g166: ArcOfCircle CenterX=-14.8377 CenterY=-4.58399 CenterZ=0 NormalX=0 NormalY=0 NormalZ=1 AngleXU=1.82212 Radius=0.15 StartAngle=0 EndAngle=1.5708
    g167: LineSegment StartX=-14.9829 StartY=-4.62129 StartZ=0 EndX=-14.8378 EndY=-5.06805 EndZ=0
    g168: ArcOfCircle CenterX=-14.6983 CenterY=-5.01283 CenterZ=0 NormalX=0 NormalY=0 NormalZ=1 AngleXU=-2.7646 Radius=0.15 StartAngle=0 EndAngle=1.5708
    g169: ArcOfCircle CenterX=-14.4391 CenterY=-6.60736 CenterZ=0 NormalX=0 NormalY=0 NormalZ=-1 AngleXU=1.4315 Radius=1.46929 StartAngle=0 EndAngle=0.255762
    g170: ArcOfCircle CenterX=-14.3844 CenterY=-5.6952 CenterZ=0 NormalX=0 NormalY=0 NormalZ=-1 AngleXU=1.77984 Radius=0.559359 StartAngle=0 EndAngle=1.96953
    g171: ArcOfCircle CenterX=-15.0487 CenterY=-5.06768 CenterZ=0 NormalX=0 NormalY=0 NormalZ=-1 AngleXU=-2.44125 Radius=1.46929 StartAngle=0 EndAngle=0.255762
    g172: ArcOfCircle CenterX=-14.1461 CenterY=-6.40749 CenterZ=0 NormalX=0 NormalY=0 NormalZ=1 AngleXU=1.94779 Radius=0.15 StartAngle=0 EndAngle=1.5708
    g173: LineSegment StartX=-14.2856 StartY=-6.46271 StartZ=0 EndX=-14.0856 EndY=-6.88775 EndZ=0
    g174: ArcOfCircle CenterX=-13.9541 CenterY=-6.81549 CenterZ=0 NormalX=0 NormalY=0 NormalZ=1 AngleXU=-2.63894 Radius=0.15 StartAngle=0 EndAngle=1.5708
    g175: ArcOfCircle CenterX=-13.4971 CenterY=-8.36496 CenterZ=0 NormalX=0 NormalY=0 NormalZ=-1 AngleXU=1.30584 Radius=1.46929 StartAngle=0 EndAngle=0.255762
    g176: ArcOfCircle CenterX=-13.5572 CenterY=-7.45314 CenterZ=0 NormalX=0 NormalY=0 NormalZ=-1 AngleXU=1.65417 Radius=0.559359 StartAngle=0 EndAngle=1.96953
    g177: ArcOfCircle CenterX=-14.2949 CenterY=-6.91383 CenterZ=0 NormalX=0 NormalY=0 NormalZ=-1 AngleXU=-2.56691 Radius=1.46929 StartAngle=0 EndAngle=0.255762
    g178: ArcOfCircle CenterX=-13.2315 CenterY=-8.12995 CenterZ=0 NormalX=0 NormalY=0 NormalZ=1 AngleXU=2.07345 Radius=0.15 StartAngle=0 EndAngle=1.5708
    g179: LineSegment StartX=-13.363 StartY=-8.20221 StartZ=0 EndX=-13.1113 EndY=-8.59883 EndZ=0
    g180: ArcOfCircle CenterX=-12.9899 CenterY=-8.51066 CenterZ=0 NormalX=0 NormalY=0 NormalZ=1 AngleXU=-2.51327 Radius=0.15 StartAngle=0 EndAngle=1.5708
    g181: ArcOfCircle CenterX=-12.3423 CenterY=-9.99063 CenterZ=0 NormalX=0 NormalY=0 NormalZ=-1 AngleXU=1.18017 Radius=1.46929 StartAngle=0 EndAngle=0.255762
    g182: ArcOfCircle CenterX=-12.5162 CenterY=-9.09354 CenterZ=0 NormalX=0 NormalY=0 NormalZ=-1 AngleXU=1.52851 Radius=0.559359 StartAngle=0 EndAngle=1.96953
    g183: ArcOfCircle CenterX=-13.3156 CenterY=-8.65093 CenterZ=0 NormalX=0 NormalY=0 NormalZ=-1 AngleXU=-2.69257 Radius=1.46929 StartAngle=0 EndAngle=0.255762
    g184: ArcOfCircle CenterX=-12.1082 CenterY=-9.72419 CenterZ=0 NormalX=0 NormalY=0 NormalZ=1 AngleXU=2.19911 Radius=0.15 StartAngle=0 EndAngle=1.5708
    g185: LineSegment StartX=-12.2296 StartY=-9.81236 StartZ=0 EndX=-11.9301 EndY=-10.1743 EndZ=0
    g186: ArcOfCircle CenterX=-11.8208 CenterY=-10.0716 CenterZ=0 NormalX=0 NormalY=0 NormalZ=1 AngleXU=-2.38761 Radius=0.15 StartAngle=0 EndAngle=1.5708
    g187: ArcOfCircle CenterX=-10.9928 CenterY=-11.4588 CenterZ=0 NormalX=0 NormalY=0 NormalZ=-1 AngleXU=1.05451 Radius=1.46929 StartAngle=0 EndAngle=0.255762
    g188: ArcOfCircle CenterX=-11.2778 CenterY=-10.5905 CenterZ=0 NormalX=0 NormalY=0 NormalZ=-1 AngleXU=1.40285 Radius=0.559359 StartAngle=0 EndAngle=1.96953
    g189: ArcOfCircle CenterX=-12.1264 CenterY=-10.2516 CenterZ=0 NormalX=0 NormalY=0 NormalZ=-1 AngleXU=-2.81824 Radius=1.46929 StartAngle=0 EndAngle=0.255762
    g190: ArcOfCircle CenterX=-10.794 CenterY=-11.1651 CenterZ=0 NormalX=0 NormalY=0 NormalZ=1 AngleXU=2.32478 Radius=0.15 StartAngle=0 EndAngle=1.5708
    g191: LineSegment StartX=-10.9033 StartY=-11.2678 StartZ=0 EndX=-10.5609 EndY=-11.5893 EndZ=0
    g192: ArcOfCircle CenterX=-10.4653 CenterY=-11.4737 CenterZ=0 NormalX=0 NormalY=0 NormalZ=1 AngleXU=-2.26195 Radius=0.15 StartAngle=0 EndAngle=1.5708
    g193: ArcOfCircle CenterX=-9.46996 CenterY=-12.7462 CenterZ=0 NormalX=0 NormalY=0 NormalZ=-1 AngleXU=0.928847 Radius=1.46929 StartAngle=0 EndAngle=0.255762
    g194: ArcOfCircle CenterX=-9.86149 CenterY=-11.9205 CenterZ=0 NormalX=0 NormalY=0 NormalZ=-1 AngleXU=1.27718 Radius=0.559359 StartAngle=0 EndAngle=1.96953
    g195: ArcOfCircle CenterX=-10.7459 CenterY=-11.6906 CenterZ=0 NormalX=0 NormalY=0 NormalZ=-1 AngleXU=-2.9439 Radius=1.46929 StartAngle=0 EndAngle=0.255762
    g196: ArcOfCircle CenterX=-9.30951 CenterY=-12.4299 CenterZ=0 NormalX=0 NormalY=0 NormalZ=1 AngleXU=2.45044 Radius=0.15 StartAngle=0 EndAngle=1.5708
    g197: LineSegment StartX=-9.40513 StartY=-12.5455 StartZ=0 EndX=-9.02509 EndY=-12.8216 EndZ=0
    g198: ArcOfCircle CenterX=-8.94472 CenterY=-12.6949 CenterZ=0 NormalX=0 NormalY=0 NormalZ=1 AngleXU=-2.13628 Radius=0.15 StartAngle=0 EndAngle=1.5708
    g199: ArcOfCircle CenterX=-7.79777 CenterY=-13.8326 CenterZ=0 NormalX=0 NormalY=0 NormalZ=-1 AngleXU=0.803184 Radius=1.46929 StartAngle=0 EndAngle=0.255762
    g200: ArcOfCircle CenterX=-8.2897 CenterY=-13.0625 CenterZ=0 NormalX=0 NormalY=0 NormalZ=-1 AngleXU=1.15152 Radius=0.559359 StartAngle=0 EndAngle=1.96953
    g201: ArcOfCircle CenterX=-9.19594 CenterY=-12.9452 CenterZ=0 NormalX=0 NormalY=0 NormalZ=-1 AngleXU=-3.06956 Radius=1.46929 StartAngle=0 EndAngle=0.255762
    g202: ArcOfCircle CenterX=-7.67823 CenterY=-13.4987 CenterZ=0 NormalX=0 NormalY=0 NormalZ=1 AngleXU=2.57611 Radius=0.15 StartAngle=0 EndAngle=1.5708
    g203: LineSegment StartX=-7.7586 StartY=-13.6253 StartZ=0 EndX=-7.34696 EndY=-13.8516 EndZ=0
    g204: ArcOfCircle CenterX=-7.28309 CenterY=-13.7159 CenterZ=0 NormalX=0 NormalY=0 NormalZ=1 AngleXU=-2.01062 Radius=0.15 StartAngle=0 EndAngle=1.5708
    g205: ArcOfCircle CenterX=-6.0026 CenterY=-14.7008 CenterZ=0 NormalX=0 NormalY=0 NormalZ=-1 AngleXU=0.67752 Radius=1.46929 StartAngle=0 EndAngle=0.255762
    g206: ArcOfCircle CenterX=-6.58717 CenterY=-13.9984 CenterZ=0 NormalX=0 NormalY=0 NormalZ=-1 AngleXU=1.02586 Radius=0.559359 StartAngle=0 EndAngle=1.96953
    g207: ArcOfCircle CenterX=-7.50096 CenterY=-13.9957 CenterZ=0 NormalX=0 NormalY=0 NormalZ=-1 AngleXU=3.08796 Radius=1.46929 StartAngle=0 EndAngle=0.255762
    g208: ArcOfCircle CenterX=-5.92585 CenterY=-14.3546 CenterZ=0 NormalX=0 NormalY=0 NormalZ=1 AngleXU=2.70177 Radius=0.15 StartAngle=0 EndAngle=1.5708
    g209: LineSegment StartX=-5.98972 StartY=-14.4903 StartZ=0 EndX=-5.55296 EndY=-14.6632 EndZ=0
    g210: ArcOfCircle CenterX=-5.50661 CenterY=-14.5205 CenterZ=0 NormalX=0 NormalY=0 NormalZ=1 AngleXU=-1.88496 Radius=0.15 StartAngle=0 EndAngle=1.5708
    g211: ArcOfCircle CenterX=-4.11277 CenterY=-15.3372 CenterZ=0 NormalX=0 NormalY=0 NormalZ=-1 AngleXU=0.551856 Radius=1.46929 StartAngle=0 EndAngle=0.255762
    g212: ArcOfCircle CenterX=-4.78076 CenterY=-14.7137 CenterZ=0 NormalX=0 NormalY=0 NormalZ=-1 AngleXU=0.900192 Radius=0.559359 StartAngle=0 EndAngle=1.96953
    g213: ArcOfCircle CenterX=-5.68768 CenterY=-14.8255 CenterZ=0 NormalX=0 NormalY=0 NormalZ=-1 AngleXU=2.96229 Radius=1.46929 StartAngle=0 EndAngle=0.255762
    g214: ArcOfCircle CenterX=-4.08002 CenterY=-14.9841 CenterZ=0 NormalX=0 NormalY=0 NormalZ=1 AngleXU=2.82743 Radius=0.15 StartAngle=0 EndAngle=1.5708
    g215: LineSegment StartX=-4.12638 StartY=-15.1267 StartZ=0 EndX=-3.67139 EndY=-15.2436 EndZ=0
    g216: ArcOfCircle CenterX=-3.64328 CenterY=-15.0962 CenterZ=0 NormalX=0 NormalY=0 NormalZ=1 AngleXU=-1.75929 Radius=0.15 StartAngle=0 EndAngle=1.5708
    g217: ArcOfCircle CenterX=-2.15808 CenterY=-15.7317 CenterZ=0 NormalX=0 NormalY=0 NormalZ=-1 AngleXU=0.426193 Radius=1.46929 StartAngle=0 EndAngle=0.255762
    g218: ArcOfCircle CenterX=-2.89895 CenterY=-15.1968 CenterZ=0 NormalX=0 NormalY=0 NormalZ=-1 AngleXU=0.774528 Radius=0.559359 StartAngle=0 EndAngle=1.96953
    g219: ArcOfCircle CenterX=-3.78471 CenterY=-15.4214 CenterZ=0 NormalX=0 NormalY=0 NormalZ=-1 AngleXU=2.83663 Radius=1.46929 StartAngle=0 EndAngle=0.255762
    g220: ArcOfCircle CenterX=-2.16985 CenterY=-15.3773 CenterZ=0 NormalX=0 NormalY=0 NormalZ=1 AngleXU=2.9531 Radius=0.15 StartAngle=0 EndAngle=1.5708
    g221: LineSegment StartX=-2.19796 StartY=-15.5246 StartZ=0 EndX=-1.73191 EndY=-15.5835 EndZ=0
    g222: ArcOfCircle CenterX=-1.72249 CenterY=-15.4338 CenterZ=0 NormalX=0 NormalY=0 NormalZ=1 AngleXU=-1.63363 Radius=0.15 StartAngle=0 EndAngle=1.5708
    g223: ArcOfCircle CenterX=-0.169352 CenterY=-15.8782 CenterZ=0 NormalX=0 NormalY=0 NormalZ=-1 AngleXU=0.300529 Radius=1.46929 StartAngle=0 EndAngle=0.255762
    g224: ArcOfCircle CenterX=-0.971423 CenterY=-15.4403 CenterZ=0 NormalX=0 NormalY=0 NormalZ=-1 AngleXU=0.648865 Radius=0.559359 StartAngle=0 EndAngle=1.96953
    g225: ArcOfCircle CenterX=-1.82204 CenterY=-15.7742 CenterZ=0 NormalX=0 NormalY=0 NormalZ=-1 AngleXU=2.71097 Radius=1.46929 StartAngle=0 EndAngle=0.255762
    g226: ArcOfCircle CenterX=-0.225455 CenterY=-15.528 CenterZ=0 NormalX=0 NormalY=0 NormalZ=1 AngleXU=3.07876 Radius=0.15 StartAngle=0 EndAngle=1.5708
    g227: LineSegment StartX=-0.234873 StartY=-15.6777 StartZ=0 EndX=0.234873 EndY=-15.6777 EndZ=0
    g228: ArcOfCircle CenterX=0.225455 CenterY=-15.528 CenterZ=0 NormalX=0 NormalY=0 NormalZ=1 AngleXU=-1.50796 Radius=0.15 StartAngle=0 EndAngle=1.5708
    g229: ArcOfCircle CenterX=1.82204 CenterY=-15.7742 CenterZ=0 NormalX=0 NormalY=0 NormalZ=-1 AngleXU=0.174865 Radius=1.46929 StartAngle=0 EndAngle=0.255762
    g230: ArcOfCircle CenterX=0.971423 CenterY=-15.4403 CenterZ=0 NormalX=0 NormalY=0 NormalZ=-1 AngleXU=0.523201 Radius=0.559359 StartAngle=0 EndAngle=1.96953
    g231: ArcOfCircle CenterX=0.169352 CenterY=-15.8782 CenterZ=0 NormalX=0 NormalY=0 NormalZ=-1 AngleXU=2.5853 Radius=1.46929 StartAngle=0 EndAngle=0.255762
    g232: ArcOfCircle CenterX=1.72249 CenterY=-15.4338 CenterZ=0 NormalX=0 NormalY=0 NormalZ=1 AngleXU=-3.07876 Radius=0.15 StartAngle=0 EndAngle=1.5708
    g233: LineSegment StartX=1.73191 StartY=-15.5835 StartZ=0 EndX=2.19796 EndY=-15.5246 EndZ=0
    g234: ArcOfCircle CenterX=2.16985 CenterY=-15.3773 CenterZ=0 NormalX=0 NormalY=0 NormalZ=1 AngleXU=-1.3823 Radius=0.15 StartAngle=0 EndAngle=1.5708
    g235: ArcOfCircle CenterX=3.78471 CenterY=-15.4214 CenterZ=0 NormalX=0 NormalY=0 NormalZ=-1 AngleXU=0.0492015 Radius=1.46929 StartAngle=0 EndAngle=0.255762
    g236: ArcOfCircle CenterX=2.89895 CenterY=-15.1968 CenterZ=0 NormalX=0 NormalY=0 NormalZ=-1 AngleXU=0.397537 Radius=0.559359 StartAngle=0 EndAngle=1.96953
    g237: ArcOfCircle CenterX=2.15808 CenterY=-15.7317 CenterZ=0 NormalX=0 NormalY=0 NormalZ=-1 AngleXU=2.45964 Radius=1.46929 StartAngle=0 EndAngle=0.255762
    g238: ArcOfCircle CenterX=3.64328 CenterY=-15.0962 CenterZ=0 NormalX=0 NormalY=0 NormalZ=1 AngleXU=-2.9531 Radius=0.15 StartAngle=0 EndAngle=1.5708
    g239: LineSegment StartX=3.67139 StartY=-15.2436 StartZ=0 EndX=4.12638 EndY=-15.1267 EndZ=0
    g240: ArcOfCircle CenterX=4.08002 CenterY=-14.9841 CenterZ=0 NormalX=0 NormalY=0 NormalZ=1 AngleXU=-1.25664 Radius=0.15 StartAngle=0 EndAngle=1.5708
    g241: ArcOfCircle CenterX=5.68768 CenterY=-14.8255 CenterZ=0 NormalX=0 NormalY=0 NormalZ=-1 AngleXU=-0.0764622 Radius=1.46929 StartAngle=0 EndAngle=0.255762
    g242: ArcOfCircle CenterX=4.78076 CenterY=-14.7137 CenterZ=0 NormalX=0 NormalY=0 NormalZ=-1 AngleXU=0.271874 Radius=0.559359 StartAngle=0 EndAngle=1.96953
    g243: ArcOfCircle CenterX=4.11277 CenterY=-15.3372 CenterZ=0 NormalX=0 NormalY=0 NormalZ=-1 AngleXU=2.33397 Radius=1.46929 StartAngle=0 EndAngle=0.255762
    g244: ArcOfCircle CenterX=5.50661 CenterY=-14.5205 CenterZ=0 NormalX=0 NormalY=0 NormalZ=1 AngleXU=-2.82743 Radius=0.15 StartAngle=0 EndAngle=1.5708
    g245: LineSegment StartX=5.55296 StartY=-14.6632 StartZ=0 EndX=5.98972 EndY=-14.4903 EndZ=0
    g246: ArcOfCircle CenterX=5.92585 CenterY=-14.3546 CenterZ=0 NormalX=0 NormalY=0 NormalZ=1 AngleXU=-1.13097 Radius=0.15 StartAngle=0 EndAngle=1.5708
    g247: ArcOfCircle CenterX=7.50096 CenterY=-13.9957 CenterZ=0 NormalX=0 NormalY=0 NormalZ=-1 AngleXU=-0.202126 Radius=1.46929 StartAngle=0 EndAngle=0.255762
    g248: ArcOfCircle CenterX=6.58717 CenterY=-13.9984 CenterZ=0 NormalX=0 NormalY=0 NormalZ=-1 AngleXU=0.14621 Radius=0.559359 StartAngle=0 EndAngle=1.96953
    g249: ArcOfCircle CenterX=6.0026 CenterY=-14.7008 CenterZ=0 NormalX=0 NormalY=0 NormalZ=-1 AngleXU=2.20831 Radius=1.46929 StartAngle=0 EndAngle=0.255762
    g250: ArcOfCircle CenterX=7.28309 CenterY=-13.7159 CenterZ=0 NormalX=0 NormalY=0 NormalZ=1 AngleXU=-2.70177 Radius=0.15 StartAngle=0 EndAngle=1.5708
    g251: LineSegment StartX=7.34696 StartY=-13.8516 StartZ=0 EndX=7.7586 EndY=-13.6253 EndZ=0
    g252: ArcOfCircle CenterX=7.67823 CenterY=-13.4987 CenterZ=0 NormalX=0 NormalY=0 NormalZ=1 AngleXU=-1.00531 Radius=0.15 StartAngle=0 EndAngle=1.5708
    g253: ArcOfCircle CenterX=9.19594 CenterY=-12.9452 CenterZ=0 NormalX=0 NormalY=0 NormalZ=-1 AngleXU=-0.32779 Radius=1.46929 StartAngle=0 EndAngle=0.255762
    g254: ArcOfCircle CenterX=8.2897 CenterY=-13.0625 CenterZ=0 NormalX=0 NormalY=0 NormalZ=-1 AngleXU=0.0205461 Radius=0.559359 StartAngle=0 EndAngle=1.96953
    g255: ArcOfCircle CenterX=7.79777 CenterY=-13.8326 CenterZ=0 NormalX=0 NormalY=0 NormalZ=-1 AngleXU=2.08265 Radius=1.46929 StartAngle=0 EndAngle=0.255762
    g256: ArcOfCircle CenterX=8.94472 CenterY=-12.6949 CenterZ=0 NormalX=0 NormalY=0 NormalZ=1 AngleXU=-2.57611 Radius=0.15 StartAngle=0 EndAngle=1.5708
    g257: LineSegment StartX=9.02509 StartY=-12.8216 StartZ=0 EndX=9.40513 EndY=-12.5455 EndZ=0
    g258: ArcOfCircle CenterX=9.30951 CenterY=-12.4299 CenterZ=0 NormalX=0 NormalY=0 NormalZ=1 AngleXU=-0.879646 Radius=0.15 StartAngle=0 EndAngle=1.5708
    g259: ArcOfCircle CenterX=10.7459 CenterY=-11.6906 CenterZ=0 NormalX=0 NormalY=0 NormalZ=-1 AngleXU=-0.453453 Radius=1.46929 StartAngle=0 EndAngle=0.255762
    g260: ArcOfCircle CenterX=9.86149 CenterY=-11.9205 CenterZ=0 NormalX=0 NormalY=0 NormalZ=-1 AngleXU=-0.105118 Radius=0.559359 StartAngle=0 EndAngle=1.96953
    g261: ArcOfCircle CenterX=9.46996 CenterY=-12.7462 CenterZ=0 NormalX=0 NormalY=0 NormalZ=-1 AngleXU=1.95698 Radius=1.46929 StartAngle=0 EndAngle=0.255762
    g262: ArcOfCircle CenterX=10.4653 CenterY=-11.4737 CenterZ=0 NormalX=0 NormalY=0 NormalZ=1 AngleXU=-2.45044 Radius=0.15 StartAngle=0 EndAngle=1.5708
    g263: LineSegment StartX=10.5609 StartY=-11.5893 StartZ=0 EndX=10.9033 EndY=-11.2678 EndZ=0
    g264: ArcOfCircle CenterX=10.794 CenterY=-11.1651 CenterZ=0 NormalX=0 NormalY=0 NormalZ=1 AngleXU=-0.753982 Radius=0.15 StartAngle=0 EndAngle=1.5708
    g265: ArcOfCircle CenterX=12.1264 CenterY=-10.2516 CenterZ=0 NormalX=0 NormalY=0 NormalZ=-1 AngleXU=-0.579117 Radius=1.46929 StartAngle=0 EndAngle=0.255762
    g266: ArcOfCircle CenterX=11.2778 CenterY=-10.5905 CenterZ=0 NormalX=0 NormalY=0 NormalZ=-1 AngleXU=-0.230781 Radius=0.559359 StartAngle=0 EndAngle=1.96953
    g267: ArcOfCircle CenterX=10.9928 CenterY=-11.4588 CenterZ=0 NormalX=0 NormalY=0 NormalZ=-1 AngleXU=1.83132 Radius=1.46929 StartAngle=0 EndAngle=0.255762
    g268: ArcOfCircle CenterX=11.8208 CenterY=-10.0716 CenterZ=0 NormalX=0 NormalY=0 NormalZ=1 AngleXU=-2.32478 Radius=0.15 StartAngle=0 EndAngle=1.5708
    g269: LineSegment StartX=11.9301 StartY=-10.1743 StartZ=0 EndX=12.2296 EndY=-9.81236 EndZ=0
    g270: ArcOfCircle CenterX=12.1082 CenterY=-9.72419 CenterZ=0 NormalX=0 NormalY=0 NormalZ=1 AngleXU=-0.628319 Radius=0.15 StartAngle=0 EndAngle=1.5708
    g271: ArcOfCircle CenterX=13.3156 CenterY=-8.65093 CenterZ=0 NormalX=0 NormalY=0 NormalZ=-1 AngleXU=-0.704781 Radius=1.46929 StartAngle=0 EndAngle=0.255762
    g272: ArcOfCircle CenterX=12.5162 CenterY=-9.09354 CenterZ=0 NormalX=0 NormalY=0 NormalZ=-1 AngleXU=-0.356445 Radius=0.559359 StartAngle=0 EndAngle=1.96953
    g273: ArcOfCircle CenterX=12.3423 CenterY=-9.99063 CenterZ=0 NormalX=0 NormalY=0 NormalZ=-1 AngleXU=1.70566 Radius=1.46929 StartAngle=0 EndAngle=0.255762
    g274: ArcOfCircle CenterX=12.9899 CenterY=-8.51066 CenterZ=0 NormalX=0 NormalY=0 NormalZ=1 AngleXU=-2.19911 Radius=0.15 StartAngle=0 EndAngle=1.5708
    g275: LineSegment StartX=13.1113 StartY=-8.59883 StartZ=0 EndX=13.363 EndY=-8.20221 EndZ=0
    g276: ArcOfCircle CenterX=13.2315 CenterY=-8.12995 CenterZ=0 NormalX=0 NormalY=0 NormalZ=1 AngleXU=-0.502655 Radius=0.15 StartAngle=0 EndAngle=1.5708
    g277: ArcOfCircle CenterX=14.2949 CenterY=-6.91383 CenterZ=0 NormalX=0 NormalY=0 NormalZ=-1 AngleXU=-0.830444 Radius=1.46929 StartAngle=0 EndAngle=0.255762
    g278: ArcOfCircle CenterX=13.5572 CenterY=-7.45314 CenterZ=0 NormalX=0 NormalY=0 NormalZ=-1 AngleXU=-0.482109 Radius=0.559359 StartAngle=0 EndAngle=1.96953
    g279: ArcOfCircle CenterX=13.4971 CenterY=-8.36496 CenterZ=0 NormalX=0 NormalY=0 NormalZ=-1 AngleXU=1.57999 Radius=1.46929 StartAngle=0 EndAngle=0.255762
    g280: ArcOfCircle CenterX=13.9541 CenterY=-6.81549 CenterZ=0 NormalX=0 NormalY=0 NormalZ=1 AngleXU=-2.07345 Radius=0.15 StartAngle=0 EndAngle=1.5708
    g281: LineSegment StartX=14.0856 StartY=-6.88775 StartZ=0 EndX=14.2856 EndY=-6.46271 EndZ=0
    g282: ArcOfCircle CenterX=14.1461 CenterY=-6.40749 CenterZ=0 NormalX=0 NormalY=0 NormalZ=1 AngleXU=-0.376991 Radius=0.15 StartAngle=0 EndAngle=1.5708
    g283: ArcOfCircle CenterX=15.0487 CenterY=-5.06768 CenterZ=0 NormalX=0 NormalY=0 NormalZ=-1 AngleXU=-0.956108 Radius=1.46929 StartAngle=0 EndAngle=0.255762
    g284: ArcOfCircle CenterX=14.3844 CenterY=-5.6952 CenterZ=0 NormalX=0 NormalY=0 NormalZ=-1 AngleXU=-0.607772 Radius=0.559359 StartAngle=0 EndAngle=1.96953
    g285: ArcOfCircle CenterX=14.4391 CenterY=-6.60736 CenterZ=0 NormalX=0 NormalY=0 NormalZ=-1 AngleXU=1.45433 Radius=1.46929 StartAngle=0 EndAngle=0.255762
    g286: ArcOfCircle CenterX=14.6983 CenterY=-5.01283 CenterZ=0 NormalX=0 NormalY=0 NormalZ=1 AngleXU=-1.94779 Radius=0.15 StartAngle=0 EndAngle=1.5708
    g287: LineSegment StartX=14.8378 StartY=-5.06805 StartZ=0 EndX=14.9829 EndY=-4.62129 EndZ=0
    g288: ArcOfCircle CenterX=14.8377 CenterY=-4.58399 CenterZ=0 NormalX=0 NormalY=0 NormalZ=1 AngleXU=-0.251327 Radius=0.15 StartAngle=0 EndAngle=1.5708
    g289: ArcOfCircle CenterX=15.5652 CenterY=-3.14162 CenterZ=0 NormalX=0 NormalY=0 NormalZ=-1 AngleXU=-1.08177 Radius=1.46929 StartAngle=0 EndAngle=0.255762
    g290: ArcOfCircle CenterX=14.9848 CenterY=-3.84744 CenterZ=0 NormalX=0 NormalY=0 NormalZ=-1 AngleXU=-0.733436 Radius=0.559359 StartAngle=0 EndAngle=1.96953
    g291: ArcOfCircle CenterX=15.1534 CenterY=-4.74556 CenterZ=0 NormalX=0 NormalY=0 NormalZ=-1 AngleXU=1.32866 Radius=1.46929 StartAngle=0 EndAngle=0.255762
    g292: ArcOfCircle CenterX=15.2107 CenterY=-3.13111 CenterZ=0 NormalX=0 NormalY=0 NormalZ=1 AngleXU=-1.82212 Radius=0.15 StartAngle=0 EndAngle=1.5708
    g293: LineSegment StartX=15.356 StartY=-3.16842 StartZ=0 EndX=15.444 EndY=-2.70699 EndZ=0
    g294: ArcOfCircle CenterX=15.2952 CenterY=-2.68819 CenterZ=0 NormalX=0 NormalY=0 NormalZ=1 AngleXU=-0.125664 Radius=0.15 StartAngle=0 EndAngle=1.5708
    g295: ArcOfCircle CenterX=15.8362 CenterY=-1.16602 CenterZ=0 NormalX=0 NormalY=0 NormalZ=-1 AngleXU=-1.20744 Radius=1.46929 StartAngle=0 EndAngle=0.255762
    g296: ArcOfCircle CenterX=15.3489 CenterY=-1.93901 CenterZ=0 NormalX=0 NormalY=0 NormalZ=-1 AngleXU=-0.8591 Radius=0.559359 StartAngle=0 EndAngle=1.96953
    g297: ArcOfCircle CenterX=15.6286 CenterY=-2.80892 CenterZ=0 NormalX=0 NormalY=0 NormalZ=-1 AngleXU=1.203 Radius=1.46929 StartAngle=0 EndAngle=0.255762
    g298: ArcOfCircle CenterX=15.4832 CenterY=-1.20002 CenterZ=0 NormalX=0 NormalY=0 NormalZ=1 AngleXU=-1.69646 Radius=0.15 StartAngle=0 EndAngle=1.5708
    g299: LineSegment StartX=15.632 StartY=-1.21882 StartZ=0 EndX=15.6615 EndY=-0.75 EndZ=0
    g300: Circle CenterX=0 CenterY=0 CenterZ=0 NormalX=0 NormalY=0 NormalZ=1 AngleXU=0 Radius=7.5
FEATURE [PartDesign::Pad] Pad
  Direction = (0,0,1)
  Length = 7.5
  Length2 = 10
  Placement = pos=(0,0,1) rot=(0,0,1;0rad)
  Profile = -> SketchGear
  ReferenceAxis = -> SketchGear [N_Axis]
  Refine = true
  Suppressed = false
  Type = 0
FEATURE [Sketcher::SketchObject] SketchBase
  ArcFitTolerance = 1e-06
  AttachmentOffset = pos=(0,0,-1) rot=(0,0,1;0rad)
  FullyConstrained = false
  MakeInternals = false
  MapMode = 5
  sketch-geometry (2):
    g0: Circle CenterX=0 CenterY=0 CenterZ=0 NormalX=0 NormalY=0 NormalZ=1 AngleXU=0 Radius=17.5
    g1: Circle CenterX=0 CenterY=0 CenterZ=0 NormalX=0 NormalY=0 NormalZ=1 AngleXU=0 Radius=7.5
  constraints (1):
    c: Diameter(g0) = 35
FEATURE [PartDesign::Pad] PadBase
  BaseFeature = -> Pad
  Direction = (0,0,1)
  Length = 1
  Length2 = 10
  Placement = pos=(0,0,1) rot=(0,0,1;0rad)
  Profile = -> SketchBase
  Refine = true
  Suppressed = false
  Type = 0
FEATURE [Sketcher::SketchObject] SketchTop
  ArcFitTolerance = 1e-06
  AttachmentOffset = pos=(0,0,6) rot=(0,0,1;0rad)
  FullyConstrained = false
  MakeInternals = false
  MapMode = 5
  Placement = pos=(0,0,8.5) rot=(0,0,1;0rad)
  sketch-geometry (2):
    g0: Circle CenterX=0 CenterY=0 CenterZ=0 NormalX=0 NormalY=0 NormalZ=1 AngleXU=0 Radius=17.5
    g1: Circle CenterX=0 CenterY=0 CenterZ=0 NormalX=0 NormalY=0 NormalZ=1 AngleXU=0 Radius=7.5
  constraints (1):
    c: Diameter(g0) = 35
FEATURE [PartDesign::Pad] PadTop
  BaseFeature = -> PadBase
  Direction = (0,0,1)
  Length = 1
  Length2 = 10
  Placement = pos=(0,0,1) rot=(0,0,1;0rad)
  Profile = -> SketchTop
  Refine = true
  Suppressed = false
  Type = 0
FEATURE [Sketcher::SketchObject] Sketch
  ArcFitTolerance = 1e-06
  AttachmentSupport = -> [PadTop]
  FullyConstrained = true
  MakeInternals = false
  MapMode = 5
  Placement = pos=(0,0,9.5) rot=(0,0,1;0rad)
  sketch-geometry (2):
    g0: Circle CenterX=0 CenterY=0 CenterZ=0 NormalX=0 NormalY=0 NormalZ=1 AngleXU=0 Radius=15
    g1: Circle CenterX=0 CenterY=0 CenterZ=0 NormalX=0 NormalY=0 NormalZ=1 AngleXU=0 Radius=7.5
  constraints (4):
    c: Coincident(g0,g-1)
    c: Diameter(g0) = 30
    c: Coincident(g1,g0)
    c: Diameter(g1) = 15
FEATURE [PartDesign::Pad] Pad001
  BaseFeature = -> PadTop
  Direction = (0,0,1)
  Length = 10
  Length2 = 10
  Placement = pos=(0,0,1) rot=(0,0,1;0rad)
  Profile = -> Sketch
  ReferenceAxis = -> Sketch [N_Axis]
  Refine = true
  Suppressed = false
  Type = 0
FEATURE [PartDesign::Body] Gear  label="GT2_Second_Max"
  AllowCompound = false
  Group = -> [SketchGear,Pad,SketchBase,PadBase,SketchTop,PadTop,Sketch,Pad001]
  Origin = -> Origin
  Tip = -> Pad001
